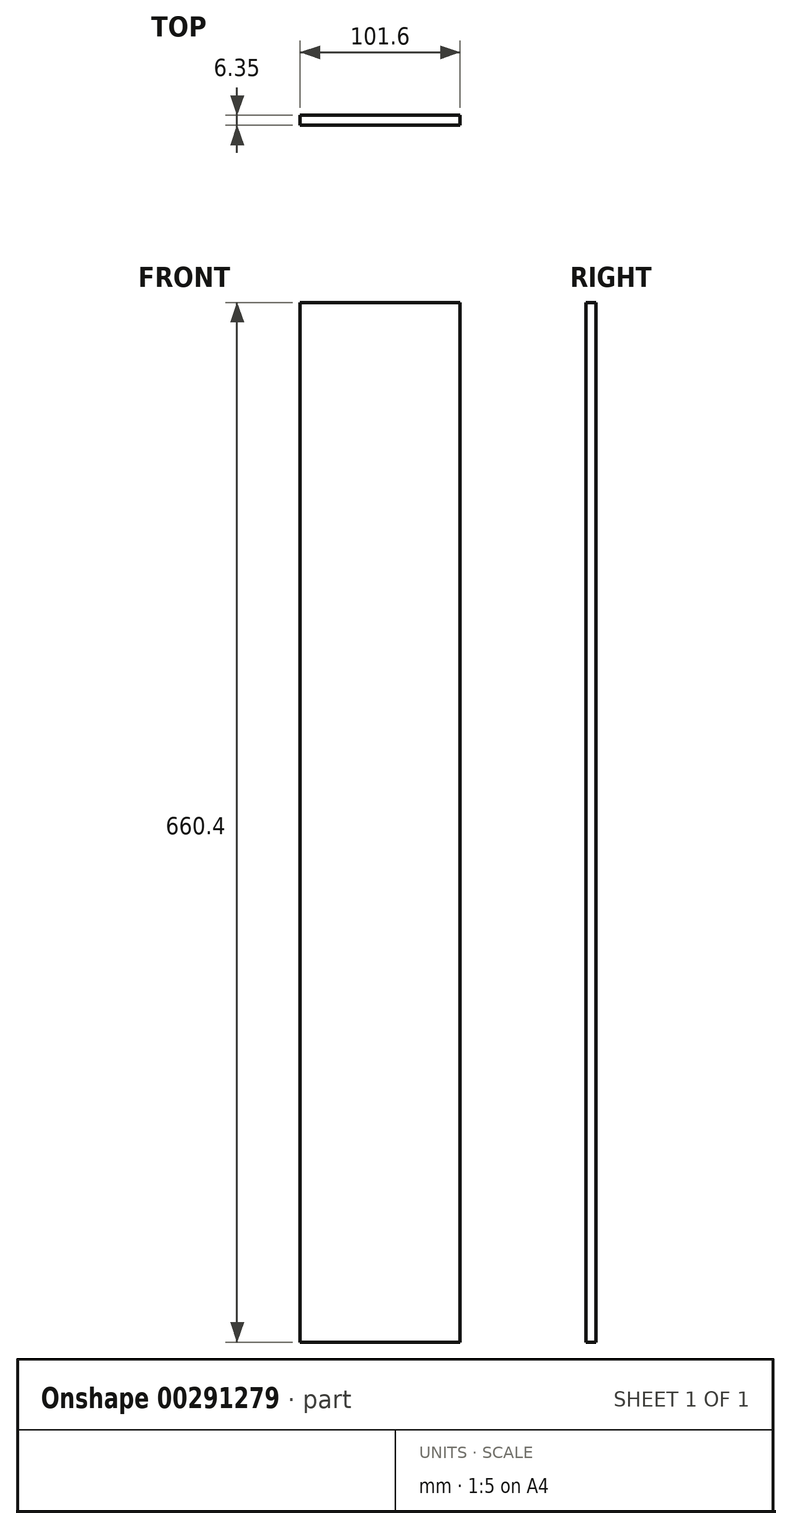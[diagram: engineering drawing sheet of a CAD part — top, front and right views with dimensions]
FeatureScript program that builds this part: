
annotation { "Feature Type Name" : "Feature", "Feature Type Description" : "" }
export const myFeature = defineFeature(function(context is Context, id is Id, definition is map)
    precondition{}
    {
        {
            var Q0;
            Q0=qCreatedBy(makeId("Front.planeOp"),FACE);
            var sketch = newSketch(context, id + "F0", { "sketchPlane" : qUnion([Q0])});
            skLineSegment(sketch, "E0", {"start": v(50.8, 330.2) * mm, "end": v(50.8, -330.2) * mm});
            skLineSegment(sketch, "E1", {"start": v(50.8, -330.2) * mm, "end": v(-50.8, -330.2) * mm});
            skLineSegment(sketch, "E2", {"start": v(-50.8, -330.2) * mm, "end": v(-50.8, 330.2) * mm});
            skLineSegment(sketch, "E3", {"start": v(-50.8, 330.2) * mm, "end": v(50.8, 330.2) * mm});
            skSolve(sketch);
        }
        {
            var Q0;
            Q0 = qSketchRegion(id + "F0", true);
            extrude(context, id + "F1", {"entities" : qUnion([Q0]), "depth" : 6.35 * mm});
        }
    });
